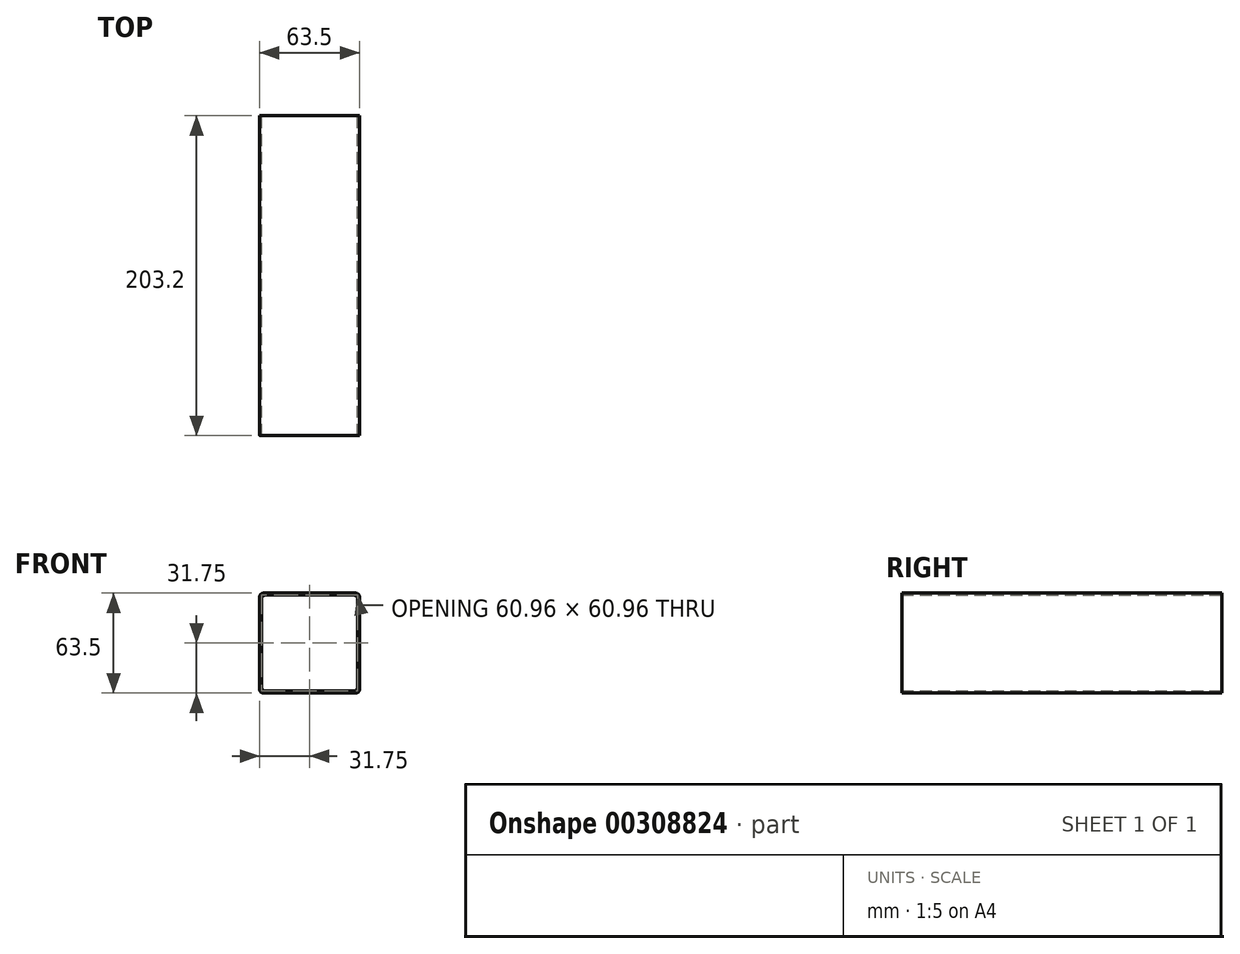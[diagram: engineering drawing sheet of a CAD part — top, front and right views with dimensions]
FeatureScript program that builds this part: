
annotation { "Feature Type Name" : "Feature", "Feature Type Description" : "" }
export const myFeature = defineFeature(function(context is Context, id is Id, definition is map)
    precondition{}
    {
        {
            var Q0;
            Q0=qCreatedBy(makeId("Front.planeOp"),FACE);
            var sketch = newSketch(context, id + "F0", { "sketchPlane" : qUnion([Q0])});
            skLineSegment(sketch, "E0.bottom", {"start": v(29.21, 31.75) * mm, "end": v(-29.21, 31.75) * mm});
            skLineSegment(sketch, "E0.top", {"start": v(29.2, -31.75) * mm, "end": v(-29.21, -31.75) * mm});
            skLineSegment(sketch, "E0.left", {"start": v(31.75, 29.21) * mm, "end": v(31.75, -29.21) * mm});
            skLineSegment(sketch, "E0.right", {"start": v(-31.75, 29.21) * mm, "end": v(-31.75, -29.21) * mm});
            skPoint(sketch, "E0.middle", {"position": v(0, 0) * mm});
            skLineSegment(sketch, "E1.bottom", {"start": v(27.94, 30.48) * mm, "end": v(-27.94, 30.48) * mm});
            skLineSegment(sketch, "E1.top", {"start": v(27.94, -30.48) * mm, "end": v(-27.94, -30.48) * mm});
            skLineSegment(sketch, "E1.left", {"start": v(30.48, 27.94) * mm, "end": v(30.48, -27.94) * mm});
            skLineSegment(sketch, "E1.right", {"start": v(-30.48, 27.94) * mm, "end": v(-30.48, -27.94) * mm});
            skPoint(sketch, "E2.visualSharp", {"position": v(-30.48, 30.48) * mm});
            skArc(sketch, "E2.filletArc", {"start": v(-27.94, 30.48) * mm, "mid": v(-29.74, 29.74) * mm, "end": v(-30.48, 27.94) * mm});
            skPoint(sketch, "E3.visualSharp", {"position": v(30.48, 30.48) * mm});
            skArc(sketch, "E3.filletArc", {"start": v(30.48, 27.94) * mm, "mid": v(29.74, 29.74) * mm, "end": v(27.94, 30.48) * mm});
            skPoint(sketch, "E4.visualSharp", {"position": v(31.75, 31.75) * mm});
            skArc(sketch, "E4.filletArc", {"start": v(31.75, 29.21) * mm, "mid": v(31, 31) * mm, "end": v(29.21, 31.75) * mm});
            skPoint(sketch, "E5.visualSharp", {"position": v(30.48, -30.48) * mm});
            skArc(sketch, "E5.filletArc", {"start": v(27.94, -30.48) * mm, "mid": v(29.74, -29.74) * mm, "end": v(30.48, -27.94) * mm});
            skPoint(sketch, "E6.visualSharp", {"position": v(31.75, -31.75) * mm});
            skArc(sketch, "E6.filletArc", {"start": v(29.2, -31.75) * mm, "mid": v(31, -31) * mm, "end": v(31.75, -29.21) * mm});
            skPoint(sketch, "E7.visualSharp", {"position": v(-30.48, -30.48) * mm});
            skArc(sketch, "E7.filletArc", {"start": v(-30.48, -27.94) * mm, "mid": v(-29.74, -29.74) * mm, "end": v(-27.94, -30.48) * mm});
            skPoint(sketch, "E8.visualSharp", {"position": v(-31.75, -31.75) * mm});
            skArc(sketch, "E8.filletArc", {"start": v(-31.75, -29.21) * mm, "mid": v(-31, -31) * mm, "end": v(-29.21, -31.75) * mm});
            skPoint(sketch, "E9.visualSharp", {"position": v(-31.75, 31.75) * mm});
            skArc(sketch, "E9.filletArc", {"start": v(-29.21, 31.75) * mm, "mid": v(-31, 31) * mm, "end": v(-31.75, 29.21) * mm});
            skSolve(sketch);
        }
        {
            var Q0;
            Q0=qSketchRegion(id+"F0",true);
            extrude(context, id + "F1", {"entities" : qUnion([Q0]), "depth" : 203.2 * mm});
        }
    });
